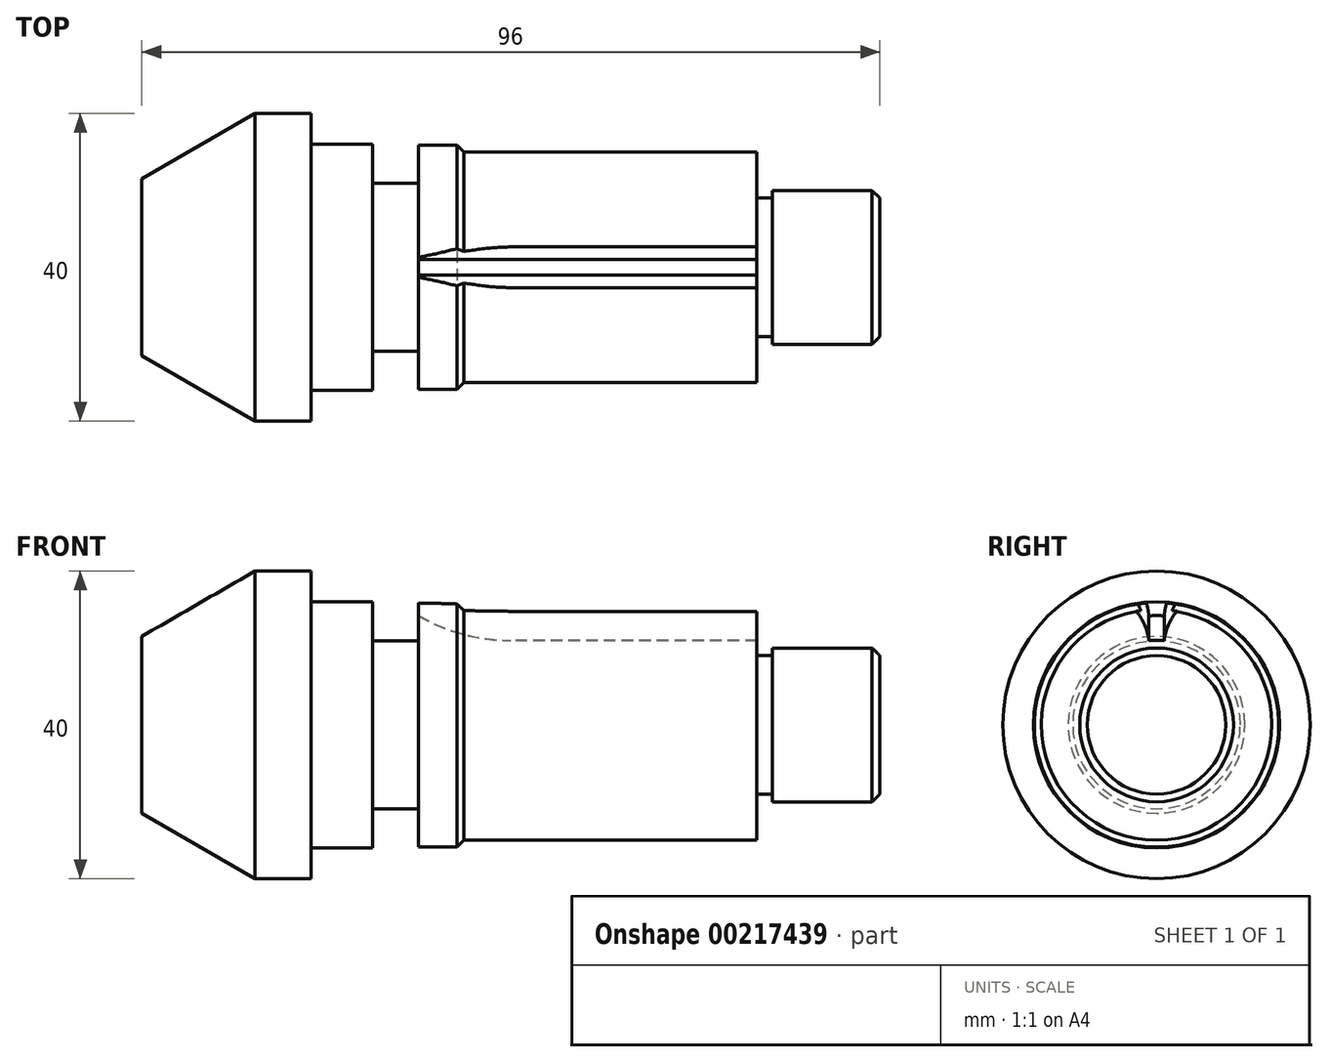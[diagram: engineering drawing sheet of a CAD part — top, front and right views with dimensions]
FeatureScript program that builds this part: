
annotation { "Feature Type Name" : "Feature", "Feature Type Description" : "" }
export const myFeature = defineFeature(function(context is Context, id is Id, definition is map)
    precondition{}
    {
        {
            var Q0;
            Q0=qCreatedBy(makeId("Front.planeOp"),FACE);
            var sketch = newSketch(context, id + "F0", { "sketchPlane" : qUnion([Q0])});
            skLineSegment(sketch, "E0", {"start": v(0, 0) * mm, "end": v(74, 0) * mm});
            skLineSegment(sketch, "E1", {"start": v(0, 20) * mm, "end": v(-7.28, 20) * mm});
            skLineSegment(sketch, "E2", {"start": v(-7.28, 20) * mm, "end": v(-22, 11.5) * mm});
            skLineSegment(sketch, "E3", {"start": v(-22, 11.5) * mm, "end": v(-22, 0) * mm});
            skLineSegment(sketch, "E4", {"start": v(0, 20) * mm, "end": v(0, 16) * mm});
            skLineSegment(sketch, "E5", {"start": v(0, 16) * mm, "end": v(8, 16) * mm});
            skLineSegment(sketch, "E6", {"start": v(8, 16) * mm, "end": v(8, 10.9) * mm});
            skLineSegment(sketch, "E7", {"start": v(8, 10.9) * mm, "end": v(14, 10.9) * mm});
            skLineSegment(sketch, "E8", {"start": v(14, 10.9) * mm, "end": v(14, 15.9) * mm});
            skLineSegment(sketch, "E9", {"start": v(14, 15.9) * mm, "end": v(19, 15.9) * mm});
            skLineSegment(sketch, "E10", {"start": v(19, 15.9) * mm, "end": v(19.9, 15) * mm});
            skLineSegment(sketch, "E11", {"start": v(19.9, 15) * mm, "end": v(58, 15) * mm});
            skLineSegment(sketch, "E12", {"start": v(58, 15) * mm, "end": v(58, 9) * mm});
            skLineSegment(sketch, "E13", {"start": v(58, 9) * mm, "end": v(60, 9) * mm});
            skLineSegment(sketch, "E14", {"start": v(60, 9) * mm, "end": v(60, 10) * mm});
            skLineSegment(sketch, "E15", {"start": v(60, 10) * mm, "end": v(73, 10) * mm});
            skLineSegment(sketch, "E16", {"start": v(73, 10) * mm, "end": v(74, 9) * mm});
            skLineSegment(sketch, "E17", {"start": v(74, 9) * mm, "end": v(74, 0) * mm});
            skLineSegment(sketch, "E18", {"start": v(-22, 0) * mm, "end": v(0, 0) * mm});
            skSolve(sketch);
        }
        {
            var Q0;
            Q0=makeQuery(id+"F0.imprint","IMPRINT",FACE,{"disambiguationData":[TD([[makeQuery(id+"F0.imprint","IMPRINT",EDGE,{"derivedFrom":sQuery(id+"F0.wireOp",EDGE,"E0")}),1.0]])]});
            var sketch = newSketch(context, id + "F1", { "sketchPlane" : qUnion([Q0])});
            skLineSegment(sketch, "E19.0", {"start": v(0, 0) * mm, "end": v(74, 0) * mm, "construction": true});
            skSolve(sketch);
        }
        {
            var Q0;
            Q0 = qSketchRegion(id + "F0", true);
            var Q1;
            Q1=sQuery(id+"F0.wireOp",EDGE,"E0");
            revolve(context, id + "F2", {"entities" : qUnion([Q0]), "axis" : qUnion([Q1]), "revolveType" : RevolveType.FULL});
        }
        {
            var Q0;
            Q0=qCreatedBy(makeId("Front.planeOp"),FACE);
            var sketch = newSketch(context, id + "F3", { "sketchPlane" : qUnion([Q0])});
            skArc(sketch, "E20", {"start": v(1, 35) * mm, "mid": v(8.32, 17.32) * mm, "end": v(26, 10) * mm});
            skLineSegment(sketch, "E21", {"start": v(26, 35) * mm, "end": v(26, 10) * mm, "construction": true});
            skLineSegment(sketch, "E22", {"start": v(26, 10) * mm, "end": v(58, 10) * mm});
            skLineSegment(sketch, "E23", {"start": v(26, 35) * mm, "end": v(1, 35) * mm, "construction": true});
            skLineSegment(sketch, "E24.1", {"start": v(58, -15) * mm, "end": v(58, 15) * mm, "construction": true});
            skSolve(sketch);
        }
        {
            var Q0;
            Q0=makeQuery(id+"F2.opRevolve","SWEPT_FACE",FACE,{"disambiguationData":[OSD([sQuery(id+"F0.wireOp",EDGE,"E12")])]});
            var sketch = newSketch(context, id + "F4", { "sketchPlane" : qUnion([Q0])});
            skArc(sketch, "E25", {"start": v(1, 10.95) * mm, "mid": v(0, 11) * mm, "end": v(-1, 10.95) * mm});
            skArc(sketch, "E26", {"start": v(3.5, 15.61) * mm, "mid": v(0, 16) * mm, "end": v(-3.5, 15.61) * mm});
            skLineSegment(sketch, "E27", {"start": v(0, 0) * mm, "end": v(0, 16) * mm, "construction": true});
            skArc(sketch, "E28", {"start": v(-1, 10.95) * mm, "mid": v(-1.8, 13.53) * mm, "end": v(-3.5, 15.61) * mm});
            skArc(sketch, "E29.MirrorCS", {"start": v(1, 10.95) * mm, "mid": v(1.8, 13.53) * mm, "end": v(3.5, 15.61) * mm});
            skSolve(sketch);
        }
        {
            var Q0;
            Q0 = qSketchRegion(id + "F4", true);
            var Q1;
            Q1=sQuery(id+"F3.wireOp",EDGE,"E22");
            var Q2;
            Q2=sQuery(id+"F3.wireOp",EDGE,"E20");
            sweep(context, id + "F5", {"operationType" : NewBodyOperationType.REMOVE, "profiles" : qUnion([Q0]), "path" : qUnion([Q1, Q2])});
        }
    });
